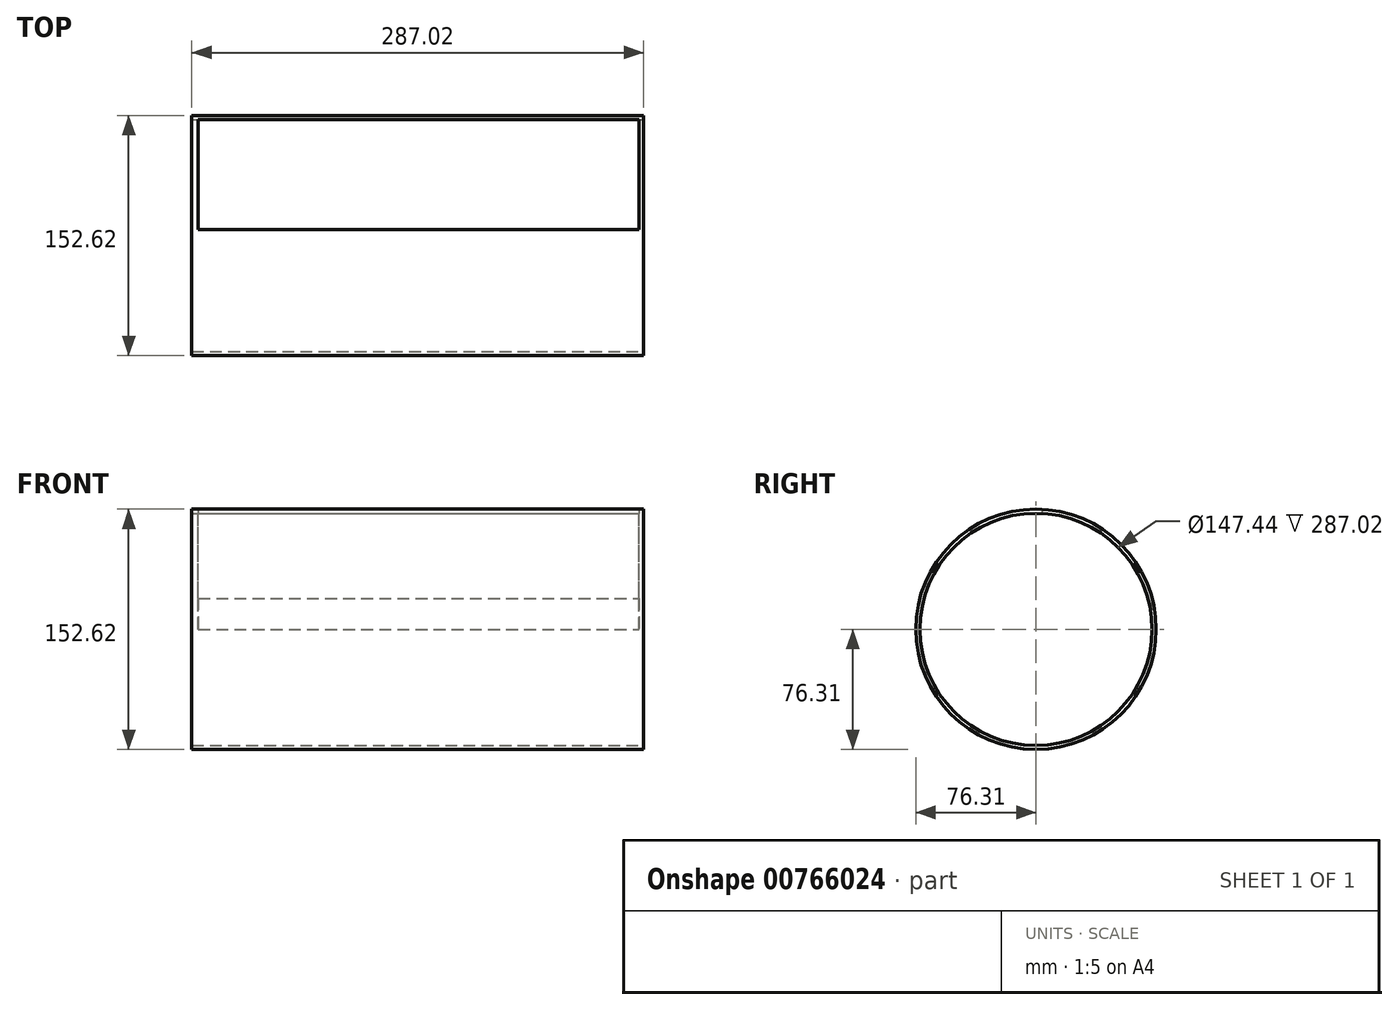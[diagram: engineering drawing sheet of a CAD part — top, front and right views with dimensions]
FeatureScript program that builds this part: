
annotation { "Feature Type Name" : "Feature", "Feature Type Description" : "" }
export const myFeature = defineFeature(function(context is Context, id is Id, definition is map)
    precondition{}
    {
        {
            var Q0;
            Q0=qCreatedBy(makeId("Right.planeOp"),FACE);
            var sketch = newSketch(context, id + "F0", { "sketchPlane" : qUnion([Q0])});
            skCircle(sketch, "E0", {"center": v(0, 0) * mm, "radius": 76.31 * mm});
            skSolve(sketch);
        }
        {
            var Q0;
            Q0 = qSketchRegion(id + "F0", true);
            extrude(context, id + "F1", {"entities" : qUnion([Q0]), "oppositeDirection" : true, "depth" : 287.02 * mm, "offsetDistance" : 25.4 * mm});
        }
        {
            var Q0;
            Q0=qCreatedBy(makeId("Right.planeOp"),FACE);
            var sketch = newSketch(context, id + "F2", { "sketchPlane" : qUnion([Q0])});
            skCircle(sketch, "E1", {"center": v(0, 0) * mm, "radius": 73.72 * mm});
            skSolve(sketch);
        }
        {
            var Q0;
            Q0 = qSketchRegion(id + "F2", true);
            extrude(context, id + "F3", {"entities" : qUnion([Q0]), "operationType" : NewBodyOperationType.REMOVE, "oppositeDirection" : true, "depth" : 1714.5 * mm, "offsetDistance" : 25.4 * mm});
        }
        {
            var Q0;
            Q0=qCreatedBy(makeId("Top.planeOp"),FACE);
            var sketch = newSketch(context, id + "F4", { "sketchPlane" : qUnion([Q0])});
            skLineSegment(sketch, "E2.bottom", {"start": v(-3.08, 73.73) * mm, "end": v(-282.9, 73.73) * mm});
            skLineSegment(sketch, "E2.top", {"start": v(-3.08, 3.88) * mm, "end": v(-282.9, 3.88) * mm});
            skLineSegment(sketch, "E2.left", {"start": v(-3.08, 73.73) * mm, "end": v(-3.08, 3.88) * mm});
            skLineSegment(sketch, "E2.right", {"start": v(-282.9, 73.73) * mm, "end": v(-282.9, 3.88) * mm});
            skSolve(sketch);
        }
        {
            var Q0;
            Q0 = qSketchRegion(id + "F4", true);
            extrude(context, id + "F5", {"entities" : qUnion([Q0]), "operationType" : NewBodyOperationType.REMOVE, "depth" : 122.43 * mm, "offsetDistance" : 25.4 * mm});
        }
    });
